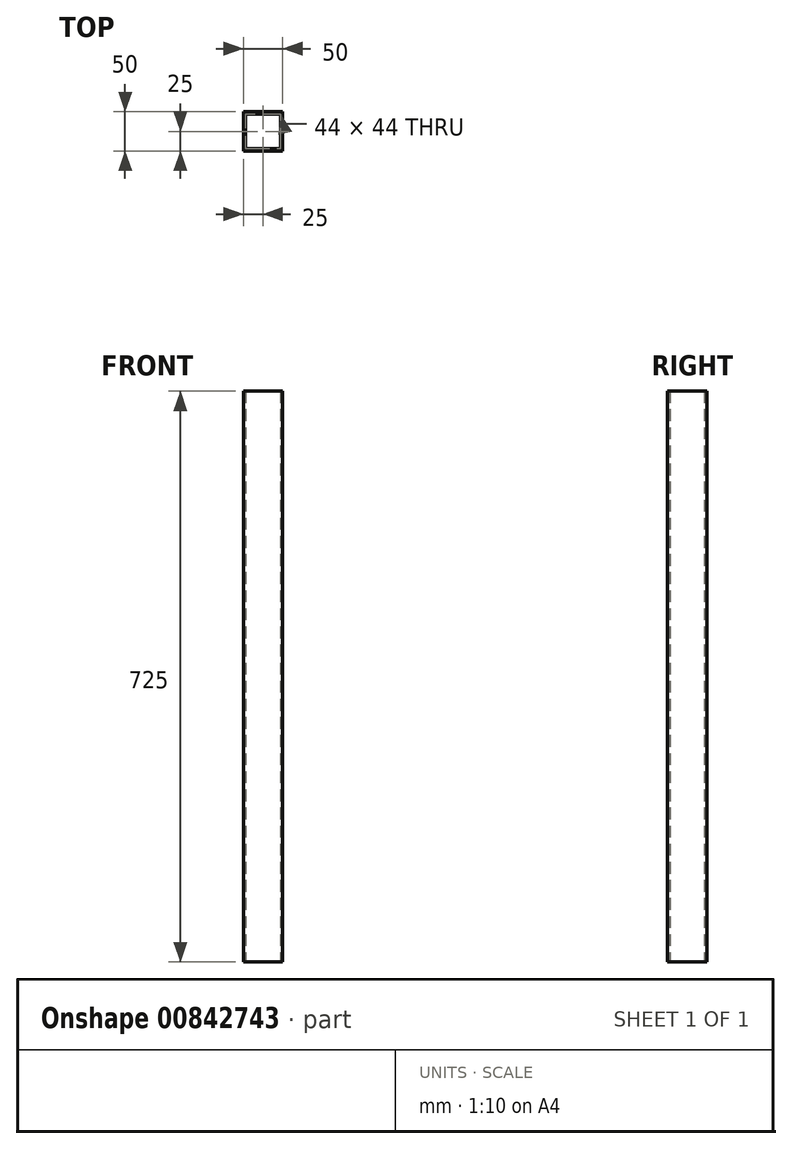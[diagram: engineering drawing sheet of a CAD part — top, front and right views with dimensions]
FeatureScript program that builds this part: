
annotation { "Feature Type Name" : "Feature", "Feature Type Description" : "" }
export const myFeature = defineFeature(function(context is Context, id is Id, definition is map)
    precondition{}
    {
        {
            var Q0;
            Q0=qCreatedBy(makeId("Top.planeOp"),FACE);
            var sketch = newSketch(context, id + "F0", { "sketchPlane" : qUnion([Q0])});
            skLineSegment(sketch, "E0.bottom", {"start": v(25, -25) * mm, "end": v(-25, -25) * mm});
            skLineSegment(sketch, "E0.top", {"start": v(25, 25) * mm, "end": v(-25, 25) * mm});
            skLineSegment(sketch, "E0.left", {"start": v(25, -25) * mm, "end": v(25, 25) * mm});
            skLineSegment(sketch, "E0.right", {"start": v(-25, -25) * mm, "end": v(-25, 25) * mm});
            skPoint(sketch, "E0.middle", {"position": v(0, 0) * mm});
            skLineSegment(sketch, "E1.0", {"start": v(-22, -22) * mm, "end": v(-22, 22) * mm});
            skLineSegment(sketch, "E1.1", {"start": v(22, -22) * mm, "end": v(-22, -22) * mm});
            skLineSegment(sketch, "E1.2", {"start": v(22, -22) * mm, "end": v(22, 22) * mm});
            skLineSegment(sketch, "E1.3", {"start": v(22, 22) * mm, "end": v(-22, 22) * mm});
            skSolve(sketch);
        }
        {
            var Q0;
            Q0=qSketchRegion(id+"F0",true);
            extrude(context, id + "F1", {"entities" : qUnion([Q0]), "depth" : 725 * mm, "offsetDistance" : 25 * mm});
        }
    });
